# Revit family: VMC-502A_Series
name_source: partatom
category: Pipe Accessories
revit_build: Autodesk Revit 2014 (Build: 20130308_1515(x64)
units: mm (PartAtom-declared; Revit-internal decimal feet)

## types (5) — shared parameters
Assembly Code = D2090800
CW Connection = No
CWP (PSI) = 250.00 psi
Default Elevation = 0"
Description = Swing-Flex Check Valve
HW Connection = No
Manufacturer = Zoeller
Material = Metal-Zoeller-Cast Iron
Price = Prices may vary. Please consult Manufacturer Representative for most up-to-date price list.
Vent Connection = No
Waste Connection = No

## per-type parameters (varying)
| type | Bolt Hole Location | Bolt Size | Flange Thickness | Height | Length | Model | No. of Bolts | Pipe Size | Width |
| 6030-0197 - 2 1/2" | 5 1/2" | 5/8" | 3/4" | 7" | 8 1/2" | VMC-525A | 4 | 2 1/2" | 5 3/16" |
| 6030-0202 - 3" | 6" | 5/8" | 13/16" | 7 1/2" | 9 1/2" | VMC-503A | 4 | 3" | 7 1/2" |
| 6030-0203 - 4" | 7 1/2" | 5/8" | 3/4" | 9" | 11 1/2" | VMC-504A | 8 | 4" | 8 1/4" |
| 6030-0180 - 6" | 9 1/2" | 3/4" | 3/4" | 11" | 14" | VMC-506C | 8 | 6" | 11 1/8" |
| 6030-0190 - 8" | 11 3/4" | 3/4" | 7/8" | 13 1/2" | 19 1/2" | VMC-508A | 8 | 8" | 16" |

## geometry (parser evidence)
native form markers: Sweep x3
no freeform markers — native parametric forms only
